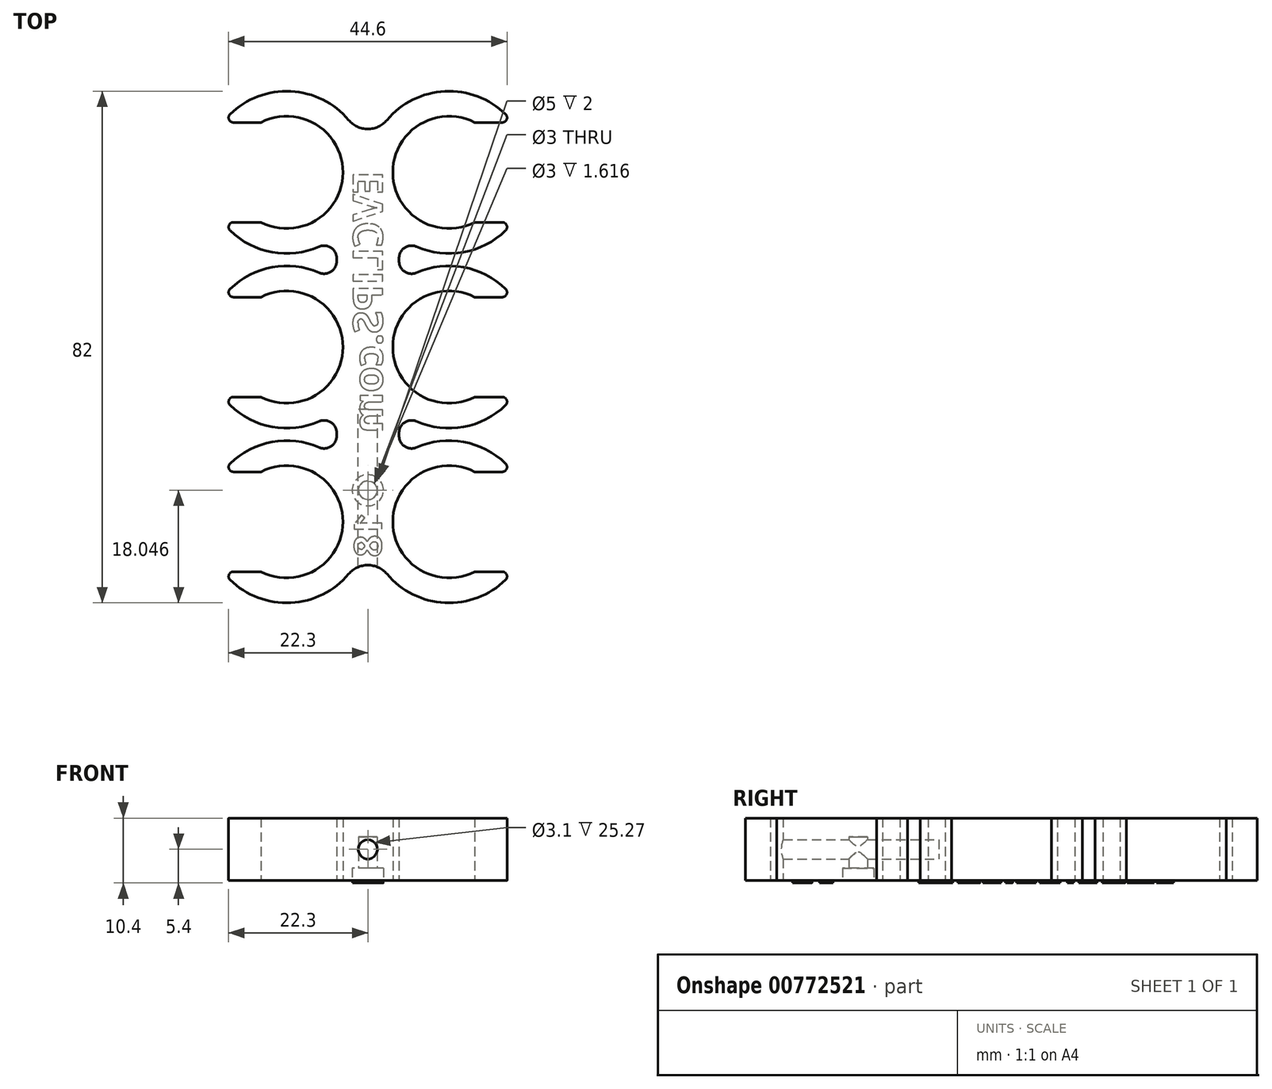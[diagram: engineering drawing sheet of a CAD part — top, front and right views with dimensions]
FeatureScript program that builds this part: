
annotation { "Feature Type Name" : "Feature", "Feature Type Description" : "" }
export const myFeature = defineFeature(function(context is Context, id is Id, definition is map)
    precondition{}
    {
        {
            var Q0;
            Q0=qCreatedBy(makeId("Top.planeOp"),FACE);
            var sketch = newSketch(context, id + "F0", { "sketchPlane" : qUnion([Q0])});
            skLineSegment(sketch, "E0.bottom", {"start": v(-5, 34.37) * mm, "end": v(5, 34.37) * mm});
            skLineSegment(sketch, "E0.top", {"start": v(-5, -34.37) * mm, "end": v(5, -34.37) * mm});
            skLineSegment(sketch, "E0.left", {"start": v(-5, 14.25) * mm, "end": v(-5, 13.75) * mm});
            skLineSegment(sketch, "E1.MirrorCS", {"start": v(5, 14.25) * mm, "end": v(5, 13.75) * mm});
            skPoint(sketch, "E2.orphan", {"position": v(-4, 34.37) * mm});
            skPoint(sketch, "E3.end.orphan", {"position": v(-4, -34.37) * mm});
            skPoint(sketch, "E4.MirrorCS.end.orphan", {"position": v(4, -34.37) * mm});
            skPoint(sketch, "E4.MirrorCS.start.orphan", {"position": v(4, 34.37) * mm});
            skLineSegment(sketch, "E5", {"start": v(-4, 34.37) * mm, "end": v(-4, -34.37) * mm, "construction": true});
            skLineSegment(sketch, "E6.MirrorCS", {"start": v(4, 34.37) * mm, "end": v(4, -34.37) * mm, "construction": true});
            skArc(sketch, "E7", {"start": v(-17.12, -8) * mm, "mid": v(-4, 0) * mm, "end": v(-17.12, 8) * mm});
            skArc(sketch, "E8", {"start": v(-22.07, -9.32) * mm, "mid": v(-15.33, -12.79) * mm, "end": v(-7.8, -11.91) * mm});
            skLineSegment(sketch, "E9", {"start": v(-13, 0) * mm, "end": v(-20, 5.66) * mm, "construction": true});
            skLineSegment(sketch, "E10", {"start": v(-20, 5.66) * mm, "end": v(-24.7, 5.66) * mm, "construction": true});
            skLineSegment(sketch, "E11", {"start": v(0, 0) * mm, "end": v(-29.1, 0) * mm, "construction": true});
            skLineSegment(sketch, "E12.MirrorCS", {"start": v(0, 0) * mm, "end": v(29.1, 0) * mm, "construction": true});
            skLineSegment(sketch, "E13", {"start": v(0, 34.37) * mm, "end": v(0, -34.37) * mm, "construction": true});
            skLineSegment(sketch, "E14", {"start": v(-13, 0) * mm, "end": v(-13, 13) * mm, "construction": true});
            skLineSegment(sketch, "E15", {"start": v(-13, 14) * mm, "end": v(-13, 13) * mm, "construction": true});
            skLineSegment(sketch, "E16", {"start": v(0, 14) * mm, "end": v(-30.87, 14) * mm, "construction": true});
            skLineSegment(sketch, "E17", {"start": v(-13, 0) * mm, "end": v(-13, -13) * mm, "construction": true});
            skLineSegment(sketch, "E18", {"start": v(-13, -14) * mm, "end": v(-13, -13) * mm, "construction": true});
            skLineSegment(sketch, "E19", {"start": v(-30.41, -14) * mm, "end": v(27.29, -14) * mm, "construction": true});
            skLineSegment(sketch, "E20", {"start": v(-13, 9) * mm, "end": v(-28.18, 9) * mm, "construction": true});
            skPoint(sketch, "E20.startSnap0", {"position": v(-13, 6.5) * mm});
            skLineSegment(sketch, "E21", {"start": v(-13, -9) * mm, "end": v(-28.18, -9) * mm, "construction": true});
            skLineSegment(sketch, "E22", {"start": v(-28.18, -9) * mm, "end": v(-28.18, 9) * mm, "construction": true});
            skLineSegment(sketch, "E23", {"start": v(-28.18, 9) * mm, "end": v(-28.18, 8) * mm, "construction": true});
            skLineSegment(sketch, "E24", {"start": v(-28.18, 8) * mm, "end": v(-28.18, 9) * mm, "construction": true});
            skLineSegment(sketch, "E25", {"start": v(-28.18, -9) * mm, "end": v(-28.18, -8) * mm, "construction": true});
            skLineSegment(sketch, "E26", {"start": v(-28.18, -8) * mm, "end": v(-28.18, -9) * mm, "construction": true});
            skLineSegment(sketch, "E27", {"start": v(-21.53, -8) * mm, "end": v(-17.12, -8) * mm});
            skLineSegment(sketch, "E28", {"start": v(-21.53, 8) * mm, "end": v(-17.12, 8) * mm});
            skArc(sketch, "E29.MirrorCS", {"start": v(22.07, -9.32) * mm, "mid": v(15.33, -12.79) * mm, "end": v(7.8, -11.91) * mm});
            skArc(sketch, "E30.MirrorCS", {"start": v(17.12, -8) * mm, "mid": v(4, 0) * mm, "end": v(17.12, 8) * mm});
            skLineSegment(sketch, "E31.MirrorCS", {"start": v(21.53, 8) * mm, "end": v(17.12, 8) * mm});
            skLineSegment(sketch, "E32.MirrorCS", {"start": v(21.53, -8) * mm, "end": v(17.12, -8) * mm});
            skArc(sketch, "E33.MirrorCS", {"start": v(-22.07, 37.32) * mm, "mid": v(-12.36, 40.98) * mm, "end": v(-3.06, 36.38) * mm});
            skArc(sketch, "E34.MirrorCS", {"start": v(-17.12, 36) * mm, "mid": v(-4, 28) * mm, "end": v(-17.12, 20) * mm});
            skLineSegment(sketch, "E35.MirrorCS", {"start": v(-21.53, 20) * mm, "end": v(-17.12, 20) * mm});
            skLineSegment(sketch, "E36.MirrorCS", {"start": v(-21.53, 36) * mm, "end": v(-17.12, 36) * mm});
            skPoint(sketch, "E37.orphan", {"position": v(-28.18, 36) * mm});
            skPoint(sketch, "E38.orphan", {"position": v(-28.18, 20) * mm});
            skPoint(sketch, "E39.orphan", {"position": v(-13, 20) * mm});
            skPoint(sketch, "E40.orphan", {"position": v(-13, 36) * mm});
            skPoint(sketch, "E41.orphan", {"position": v(13, 8) * mm});
            skPoint(sketch, "E42.orphan", {"position": v(28.18, 8) * mm});
            skPoint(sketch, "E43.orphan", {"position": v(28.18, -8) * mm});
            skPoint(sketch, "E44.orphan", {"position": v(13, -8) * mm});
            skPoint(sketch, "E45.orphan", {"position": v(-13, 8) * mm});
            skPoint(sketch, "E46.orphan", {"position": v(-13, -8) * mm});
            skArc(sketch, "E47.MirrorCS", {"start": v(-17.12, -20) * mm, "mid": v(-4, -28) * mm, "end": v(-17.12, -36) * mm});
            skArc(sketch, "E48.MirrorCS", {"start": v(-22.07, -18.68) * mm, "mid": v(-15.33, -15.21) * mm, "end": v(-7.8, -16.09) * mm});
            skLineSegment(sketch, "E49.MirrorCS", {"start": v(-21.53, -20) * mm, "end": v(-17.12, -20) * mm});
            skLineSegment(sketch, "E50.MirrorCS", {"start": v(-21.53, -36) * mm, "end": v(-17.12, -36) * mm});
            skArc(sketch, "E51.MirrorCS", {"start": v(22.07, -18.68) * mm, "mid": v(15.33, -15.21) * mm, "end": v(7.8, -16.09) * mm});
            skArc(sketch, "E52.MirrorCS", {"start": v(17.12, -20) * mm, "mid": v(4, -28) * mm, "end": v(17.12, -36) * mm});
            skLineSegment(sketch, "E53.MirrorCS", {"start": v(21.53, -20) * mm, "end": v(17.12, -20) * mm});
            skLineSegment(sketch, "E54.MirrorCS", {"start": v(21.53, -36) * mm, "end": v(17.12, -36) * mm});
            skArc(sketch, "E55.MirrorCS", {"start": v(17.12, 36) * mm, "mid": v(4, 28) * mm, "end": v(17.12, 20) * mm});
            skArc(sketch, "E56.MirrorCS", {"start": v(22.07, 37.32) * mm, "mid": v(12.36, 40.98) * mm, "end": v(3.06, 36.38) * mm});
            skLineSegment(sketch, "E57.MirrorCS", {"start": v(21.53, 20) * mm, "end": v(17.12, 20) * mm});
            skLineSegment(sketch, "E58.MirrorCS", {"start": v(21.53, 36) * mm, "end": v(17.12, 36) * mm});
            skArc(sketch, "E59.trimOffspring", {"start": v(-7.8, 16.09) * mm, "mid": v(-15.33, 15.21) * mm, "end": v(-22.07, 18.68) * mm});
            skArc(sketch, "E60.trimOffspring", {"start": v(7.8, 16.09) * mm, "mid": v(15.33, 15.21) * mm, "end": v(22.07, 18.68) * mm});
            skLineSegment(sketch, "E61.trimOffspring", {"start": v(-5, -13.75) * mm, "end": v(-5, -14.25) * mm});
            skArc(sketch, "E62.trimOffspring", {"start": v(-7.8, 11.91) * mm, "mid": v(-15.33, 12.79) * mm, "end": v(-22.07, 9.32) * mm});
            skArc(sketch, "E63.trimOffspring", {"start": v(7.8, 11.91) * mm, "mid": v(15.33, 12.79) * mm, "end": v(22.07, 9.32) * mm});
            skLineSegment(sketch, "E64.trimOffspring", {"start": v(5, -13.75) * mm, "end": v(5, -14.25) * mm});
            skArc(sketch, "E65.trimOffspring", {"start": v(3.06, -36.38) * mm, "mid": v(12.36, -40.98) * mm, "end": v(22.07, -37.32) * mm});
            skArc(sketch, "E66.trimOffspring", {"start": v(-3.06, -36.38) * mm, "mid": v(-12.36, -40.98) * mm, "end": v(-22.07, -37.32) * mm});
            skPoint(sketch, "E67.visualSharp", {"position": v(0, -28) * mm});
            skArc(sketch, "E67.filletArc", {"start": v(3.06, -36.38) * mm, "mid": v(0, -34.95) * mm, "end": v(-3.06, -36.38) * mm});
            skPoint(sketch, "E68.visualSharp", {"position": v(-5, -17.75) * mm});
            skArc(sketch, "E68.filletArc", {"start": v(-7.8, -16.09) * mm, "mid": v(-5.9, -15.93) * mm, "end": v(-5, -14.25) * mm});
            skPoint(sketch, "E69.visualSharp", {"position": v(-5, -10.25) * mm});
            skArc(sketch, "E69.filletArc", {"start": v(-5, -13.75) * mm, "mid": v(-5.9, -12.07) * mm, "end": v(-7.8, -11.91) * mm});
            skPoint(sketch, "E70.visualSharp", {"position": v(5, -17.75) * mm});
            skArc(sketch, "E70.filletArc", {"start": v(5, -14.25) * mm, "mid": v(5.9, -15.93) * mm, "end": v(7.8, -16.09) * mm});
            skPoint(sketch, "E71.visualSharp", {"position": v(5, -10.25) * mm});
            skArc(sketch, "E71.filletArc", {"start": v(7.8, -11.91) * mm, "mid": v(5.9, -12.07) * mm, "end": v(5, -13.75) * mm});
            skPoint(sketch, "E72.visualSharp", {"position": v(-5, 10.25) * mm});
            skArc(sketch, "E72.filletArc", {"start": v(-7.8, 11.91) * mm, "mid": v(-5.9, 12.07) * mm, "end": v(-5, 13.75) * mm});
            skPoint(sketch, "E73.visualSharp", {"position": v(-5, 17.75) * mm});
            skArc(sketch, "E73.filletArc", {"start": v(-5, 14.25) * mm, "mid": v(-5.9, 15.93) * mm, "end": v(-7.8, 16.09) * mm});
            skPoint(sketch, "E74.visualSharp", {"position": v(5, 10.25) * mm});
            skArc(sketch, "E74.filletArc", {"start": v(5, 13.75) * mm, "mid": v(5.9, 12.07) * mm, "end": v(7.8, 11.91) * mm});
            skPoint(sketch, "E75.visualSharp", {"position": v(5, 17.75) * mm});
            skArc(sketch, "E75.filletArc", {"start": v(7.8, 16.09) * mm, "mid": v(5.9, 15.93) * mm, "end": v(5, 14.25) * mm});
            skArc(sketch, "E76.filletArc", {"start": v(-3.06, 36.38) * mm, "mid": v(0, 34.95) * mm, "end": v(3.06, 36.38) * mm});
            skPoint(sketch, "E77.visualSharp", {"position": v(-23.25, -36) * mm});
            skArc(sketch, "E77.filletArc", {"start": v(-21.53, -36) * mm, "mid": v(-22.24, -36.48) * mm, "end": v(-22.07, -37.32) * mm});
            skPoint(sketch, "E78.visualSharp", {"position": v(-23.25, -20) * mm});
            skArc(sketch, "E78.filletArc", {"start": v(-22.07, -18.68) * mm, "mid": v(-22.24, -19.52) * mm, "end": v(-21.53, -20) * mm});
            skPoint(sketch, "E79.visualSharp", {"position": v(23.25, -36) * mm});
            skArc(sketch, "E79.filletArc", {"start": v(22.07, -37.32) * mm, "mid": v(22.24, -36.48) * mm, "end": v(21.53, -36) * mm});
            skPoint(sketch, "E80.visualSharp", {"position": v(23.25, -20) * mm});
            skArc(sketch, "E80.filletArc", {"start": v(21.53, -20) * mm, "mid": v(22.24, -19.52) * mm, "end": v(22.07, -18.68) * mm});
            skPoint(sketch, "E81.visualSharp", {"position": v(23.25, -8) * mm});
            skArc(sketch, "E81.filletArc", {"start": v(22.07, -9.32) * mm, "mid": v(22.24, -8.48) * mm, "end": v(21.53, -8) * mm});
            skPoint(sketch, "E82.visualSharp", {"position": v(23.25, 8) * mm});
            skArc(sketch, "E82.filletArc", {"start": v(21.53, 8) * mm, "mid": v(22.24, 8.48) * mm, "end": v(22.07, 9.32) * mm});
            skPoint(sketch, "E83.visualSharp", {"position": v(-23.25, 8) * mm});
            skArc(sketch, "E83.filletArc", {"start": v(-22.07, 9.32) * mm, "mid": v(-22.24, 8.48) * mm, "end": v(-21.53, 8) * mm});
            skPoint(sketch, "E84.visualSharp", {"position": v(-23.25, -8) * mm});
            skArc(sketch, "E84.filletArc", {"start": v(-21.53, -8) * mm, "mid": v(-22.24, -8.48) * mm, "end": v(-22.07, -9.32) * mm});
            skPoint(sketch, "E85.visualSharp", {"position": v(23.25, 20) * mm});
            skArc(sketch, "E85.filletArc", {"start": v(22.07, 18.68) * mm, "mid": v(22.24, 19.52) * mm, "end": v(21.53, 20) * mm});
            skPoint(sketch, "E86.visualSharp", {"position": v(-23.25, 20) * mm});
            skArc(sketch, "E86.filletArc", {"start": v(-21.53, 20) * mm, "mid": v(-22.24, 19.52) * mm, "end": v(-22.07, 18.68) * mm});
            skPoint(sketch, "E87.visualSharp", {"position": v(23.25, 36) * mm});
            skArc(sketch, "E87.filletArc", {"start": v(21.53, 36) * mm, "mid": v(22.24, 36.48) * mm, "end": v(22.07, 37.32) * mm});
            skPoint(sketch, "E88.visualSharp", {"position": v(-23.25, 36) * mm});
            skArc(sketch, "E88.filletArc", {"start": v(-22.07, 37.32) * mm, "mid": v(-22.24, 36.48) * mm, "end": v(-21.53, 36) * mm});
            skSolve(sketch);
        }
        {
            var Q0;
            Q0=makeQuery(id+"F0.imprint","IMPRINT",FACE,{"disambiguationData":[TD([[makeQuery(id+"F0.imprint","IMPRINT",EDGE,{"derivedFrom":sQuery(id+"F0.wireOp",EDGE,"E7")}),-1.0]])]});
            extrude(context, id + "F1", {"entities" : qUnion([Q0]), "depth" : 10 * mm, "offsetDistance" : 25 * mm});
        }
        {
            var Q0;
            Q0=qCreatedBy(makeId("Front.planeOp"),FACE);
            var sketch = newSketch(context, id + "F2", { "sketchPlane" : qUnion([Q0])});
            skLineSegment(sketch, "E89", {"start": v(0, 10) * mm, "end": v(0, 0) * mm, "construction": true});
            skCircle(sketch, "E90", {"center": v(0, 5) * mm, "radius": 1.55 * mm});
            skSolve(sketch);
        }
        {
            var Q0;
            Q0=qSketchRegion(id+"F2",true);
            extrude(context, id + "F3", {"entities" : qUnion([Q0]), "operationType" : NewBodyOperationType.REMOVE, "depth" : 50 * mm, "offsetDistance" : 25 * mm, "hasSecondDirection" : true, "secondDirectionOppositeDirection" : true, "secondDirectionDepth" : -10 * mm});
        }
        {
            var Q0;
            Q0=qCreatedBy(makeId("Top.planeOp"),FACE);
            var sketch = newSketch(context, id + "F4", { "sketchPlane" : qUnion([Q0])});
            skCircle(sketch, "E91", {"center": v(0, -22.95) * mm, "radius": 1.5 * mm});
            skLineSegment(sketch, "E92", {"start": v(0, -31.34) * mm, "end": v(0, -32.64) * mm, "construction": true});
            skCircle(sketch, "E93", {"center": v(0, -22.95) * mm, "radius": 2.5 * mm});
            skSolve(sketch);
        }
        {
            var Q0;
            Q0=qSketchRegion(id+"F4",true);
            extrude(context, id + "F5", {"entities" : qUnion([Q0]), "operationType" : NewBodyOperationType.REMOVE, "depth" : 2 * mm, "offsetDistance" : 25 * mm});
        }
        {
            var Q0;
            Q0=makeQuery(id+"F4.imprint","IMPRINT",FACE,{"disambiguationData":[TD([[makeQuery(id+"F4.imprint","IMPRINT",EDGE,{"derivedFrom":sQuery(id+"F4.wireOp",EDGE,"E91")}),1.0]])]});
            extrude(context, id + "F6", {"entities" : qUnion([Q0]), "operationType" : NewBodyOperationType.REMOVE, "depth" : 7 * mm, "offsetDistance" : 25 * mm});
        }
        {
            var Q0;
            {var subQ0=sQuery(id+"F0.wireOp",EDGE,"E85.filletArc");var subQ1=sQuery(id+"F0.wireOp",EDGE,"E84.filletArc");var subQ2=sQuery(id+"F0.wireOp",EDGE,"E83.filletArc");var subQ3=sQuery(id+"F0.wireOp",EDGE,"E82.filletArc");var subQ4=sQuery(id+"F0.wireOp",EDGE,"E81.filletArc");var subQ5=sQuery(id+"F0.wireOp",EDGE,"E80.filletArc");var subQ6=sQuery(id+"F0.wireOp",EDGE,"E79.filletArc");var subQ7=sQuery(id+"F0.wireOp",EDGE,"E78.filletArc");var subQ8=sQuery(id+"F0.wireOp",EDGE,"E77.filletArc");var subQ9=sQuery(id+"F0.wireOp",EDGE,"E76.filletArc");var subQ10=sQuery(id+"F0.wireOp",EDGE,"E75.filletArc");var subQ11=sQuery(id+"F0.wireOp",EDGE,"E74.filletArc");var subQ12=sQuery(id+"F0.wireOp",EDGE,"E73.filletArc");var subQ13=sQuery(id+"F0.wireOp",EDGE,"E72.filletArc");var subQ14=sQuery(id+"F0.wireOp",EDGE,"E71.filletArc");var subQ15=sQuery(id+"F0.wireOp",EDGE,"E70.filletArc");var subQ16=sQuery(id+"F0.wireOp",EDGE,"E69.filletArc");var subQ17=sQuery(id+"F0.wireOp",EDGE,"E68.filletArc");var subQ18=sQuery(id+"F0.wireOp",EDGE,"E67.filletArc");var subQ19=sQuery(id+"F0.wireOp",EDGE,"E66.trimOffspring");var subQ20=sQuery(id+"F0.wireOp",EDGE,"E65.trimOffspring");var subQ21=sQuery(id+"F0.wireOp",EDGE,"E63.trimOffspring");var subQ22=sQuery(id+"F0.wireOp",EDGE,"E62.trimOffspring");var subQ23=sQuery(id+"F0.wireOp",EDGE,"E60.trimOffspring");var subQ24=sQuery(id+"F0.wireOp",EDGE,"E59.trimOffspring");var subQ25=sQuery(id+"F0.wireOp",EDGE,"E58.MirrorCS");var subQ26=sQuery(id+"F0.wireOp",EDGE,"E57.MirrorCS");var subQ27=sQuery(id+"F0.wireOp",EDGE,"E33.MirrorCS");var subQ28=sQuery(id+"F0.wireOp",EDGE,"E32.MirrorCS");var subQ29=sQuery(id+"F0.wireOp",EDGE,"E31.MirrorCS");var subQ30=sQuery(id+"F0.wireOp",EDGE,"E30.MirrorCS");var subQ31=sQuery(id+"F0.wireOp",EDGE,"E29.MirrorCS");var subQ32=sQuery(id+"F0.wireOp",EDGE,"E34.MirrorCS");var subQ33=sQuery(id+"F0.wireOp",EDGE,"E86.filletArc");var subQ34=sQuery(id+"F0.wireOp",EDGE,"E7");var subQ35=sQuery(id+"F0.wireOp",EDGE,"E56.MirrorCS");var subQ36=sQuery(id+"F0.wireOp",EDGE,"E28");var subQ37=sQuery(id+"F0.wireOp",EDGE,"E8");var subQ38=sQuery(id+"F0.wireOp",EDGE,"E27");var subQ39=sQuery(id+"F0.wireOp",EDGE,"E35.MirrorCS");var subQ40=sQuery(id+"F0.wireOp",EDGE,"E36.MirrorCS");var subQ41=sQuery(id+"F0.wireOp",EDGE,"E47.MirrorCS");var subQ42=sQuery(id+"F0.wireOp",EDGE,"E48.MirrorCS");var subQ43=sQuery(id+"F0.wireOp",EDGE,"E49.MirrorCS");var subQ44=sQuery(id+"F0.wireOp",EDGE,"E50.MirrorCS");var subQ45=sQuery(id+"F0.wireOp",EDGE,"E51.MirrorCS");var subQ46=sQuery(id+"F0.wireOp",EDGE,"E52.MirrorCS");var subQ47=sQuery(id+"F0.wireOp",EDGE,"E53.MirrorCS");var subQ48=sQuery(id+"F0.wireOp",EDGE,"E54.MirrorCS");var subQ49=sQuery(id+"F0.wireOp",EDGE,"E55.MirrorCS");var subQ50=sQuery(id+"F0.wireOp",EDGE,"E87.filletArc");var subQ51=sQuery(id+"F0.wireOp",EDGE,"E88.filletArc");Q0=makeQuery(id+"F5.boolean.opBoolean","SPLIT",FACE,{"disambiguationData":[TD([makeQuery(id+"F1.opExtrude","SWEPT_FACE",FACE,{"disambiguationData":[OSD([subQ34])]})])],"derivedFrom":makeQuery(id+"F1.opExtrude","CAP_FACE",FACE,{"disambiguationData":[OSD([subQ34,subQ37,subQ38,subQ36,subQ31,subQ30,subQ29,subQ28,subQ27,subQ32,subQ39,subQ40,subQ41,subQ42,subQ43,subQ44,subQ45,subQ46,subQ47,subQ48,subQ49,subQ35,subQ26,subQ25,subQ24,subQ23,subQ22,subQ21,subQ20,subQ19,subQ18,subQ17,subQ16,subQ15,subQ14,subQ13,subQ12,subQ11,subQ10,subQ9,subQ8,subQ7,subQ6,subQ5,subQ4,subQ3,subQ2,subQ1,subQ0,subQ33,subQ50,subQ51])],"isStart":true})});}
            var sketch = newSketch(context, id + "F7", { "sketchPlane" : qUnion([Q0])});
            skLineSegment(sketch, "E94", {"start": v(0, -34.95) * mm, "end": v(0, 20.45) * mm, "construction": true});
            skLineSegment(sketch, "E95.bottom", {"start": v(3, 18.45) * mm, "end": v(-1.78, 18.45) * mm, "construction": true});
            skLineSegment(sketch, "E95.left", {"start": v(3, 13.7) * mm, "end": v(3, -34.95) * mm, "construction": true});
            skPoint(sketch, "E95.middle", {"position": v(1.59, -18.33) * mm});
            skLineSegment(sketch, "E96", {"start": v(3, -34.95) * mm, "end": v(3.23, -34.95) * mm, "construction": true});
            skLineSegment(sketch, "E97", {"start": v(3, -32.95) * mm, "end": v(3, -32.95) * mm});
            skText(sketch, "E98", { "text": "EVCLIPS.com\n", "fontName": "OpenSans-Bold.ttf"});
            skLineSegment(sketch, "E99", {"start": v(0, 25.45) * mm, "end": v(0, 34.95) * mm, "construction": true});
            skPoint(sketch, "E100.middle", {"position": v(0, 30.2) * mm});
            skLineSegment(sketch, "E101", {"start": v(-2.4, -26.93) * mm, "end": v(-2.4, 17.7) * mm, "construction": true});
            skLineSegment(sketch, "E102", {"start": v(-2.4, -5.5) * mm, "end": v(3, -5.5) * mm, "construction": true});
            skText(sketch, "E103", { "text": "18", "fontName": "OpenSans-Bold.ttf"});
            const initialGuessF7  = {"E98": [0.00238, -0.0282, 0, 1, 0.00478], "E103": [0.00222, 0.02659, 0, 1, 0.00445]};
            skSetInitialGuess(sketch, initialGuessF7);
            skSolve(sketch);
        }
        {
            var Q0;
            Q0=qSketchRegion(id+"F7",true);
            extrude(context, id + "F8", {"entities" : qUnion([Q0]), "operationType" : NewBodyOperationType.ADD, "depth" : 0.4 * mm, "offsetDistance" : 25 * mm});
        }
    });
